# Revit family: IEK_РозеткаСетевая_ОткрытойУстановки_Без ЗК 10А 4-хместная IP20_ОКТАВА
name_source: partatom
category: Электрические приборы
units: mm (PartAtom-declared; Revit-internal decimal feet)

## family parameters
Всегда вертикально = Да
На основе рабочей плоскости = Нет
Общий = Нет
При загрузке вырезать с полостями = Нет
Размер круглого соединителя = Использовать диаметр
Сохранять ориентацию аннотаций = Да
Тип детали = Нормальный
Точка расчета площади = Нет

## types (1)
- РС24-2-ОК
    ADSK_URL страницы изделия = https://www.iek.ru
    ADSK_Версия Revit = 2019
    ADSK_Версия семейства = 1.0
    ADSK_Группирование = III ЭЛЕКТРОУСТАНОВОЧНЫЕ И ЭЛЕКТРОМОНТАЖНЫЕ ИЗДЕЛИЯ
    ADSK_Единица измерения = шт
    ADSK_Завод-изготовитель = IEK
    ADSK_Код изделия = ERO40-K33-10-DC
    ADSK_Количество фаз = 1
    ADSK_Количество фаз числовое = 1
    ADSK_Марка = ОКТАВА
    ADSK_Масса = 0.088
    ADSK_Материал = Цвет кремовый
    ADSK_Материал наименование = Пластик
    ADSK_Наименование = Розетка 4-местная для открытой установки РС24-2-ОБ без заземляющего контакта 10А ОКТАВА кремовый IEK
    ADSK_Напряжение = 220 В
    IEK_URL = https://www.iek.ru
    IEK_Описание = Универсальный дизайн серии открытой установки "ОКТАВА" позволяет устанавливать изделия в квартирах, загородных домах, офисных и производственных помещениях.
    IEK_Цена за единицу = 387.28
    KSI_CMa_Строительные материалы = 01.7.14.03
    KSI_CPr_Строительные изделия = 20.4.03.04 20.4.03.05 20.4.03.06
    Высота = 103 мм
    Глубина = 31 мм
    Изготовитель = IEK
    Степень защиты = IP20
    Тип монтажа = Поверхность монтажа (открытая установка)
    Ширина = 103 мм
